# Revit family: Zumtobel LINELIGHT
name_source: partatom
category: Lighting Fixtures
revit_build: Autodesk Revit 2018 (Build: 20170223_1515(x64)
units: mm (PartAtom-declared; Revit-internal decimal feet)

## family parameters
Cut with Voids When Loaded = No
Host = Face
Light Source = Yes
OmniClass Number = 23.80.70.11
OmniClass Title = Luminaries for Internal Lighting
Part Type = Normal
Room Calculation Point = No
Round Connector Dimension = Use Diameter
Shared = No

## types (10) — shared parameters
Assembly Code = D5020210
Body = ZG_Metal_Aluminium
Color Filter = 16777215
Description = LED light line luminaire
Dimming Lamp Color Temperature Shift = <None>
Emit Shape Visible in Rendering = No
Height = 27 mm  [stored 0.0885827 ft]
Lamp = LED
Manufacturer = Zumtobel Lighting
URL = http://www.zumtobel.com
Voltage = 230 V
Width = 60 mm  [stored 0.19685 ft]
zero-valued in all types: Default Elevation

## per-type parameters (varying)
| type | Apparent Load | Emit from Rectangle Length | Emit from Rectangle Width | Length | Model | Photometric Web File | Tilt Angle |
| LINELIGHT L910 | 15 VA | 25 mm  [stored 0.082021 ft] | 900 mm  [stored 2.95276 ft] | 910 mm | 21013707 | 21013707_(STD_LEO).IES | 90.00° |
| AMPHIBIA S 4600 MB | 31 VA | 60 mm  [stored 0.19685 ft] | 1090 mm  [stored 3.57612 ft] | 1100 mm | 42929203 | D39911AA_AMP_S_4600-840_PC_MB.IES | -90.00° |
| AMPHIBIA L 4600 WB | 33 VA | 60 mm  [stored 0.19685 ft] | 1590 mm | 1600 mm  [stored 5.24934 ft] | 42929225 | D39805AA_AMP_L_4600-840_PC_WB.IES | -90.00° |
| AMPHIBIA L 6400 MB | 44 VA | 60 mm  [stored 0.19685 ft] | 1590 mm | 1600 mm  [stored 5.24934 ft] | 42929253 | D39911AA_AMP_L_6400-840_PC_MB.IES | -90.00° |
| AMPHIBIA L 6400 NB | 41 VA | 60 mm  [stored 0.19685 ft] | 1590 mm | 1600 mm  [stored 5.24934 ft] | 42929257 | D39907AA_AMP_L_6400-840_PC_NB.IES | -90.00° |
| AMPHIBIA L 6400 WB | 46 VA | 60 mm  [stored 0.19685 ft] | 1590 mm | 1600 mm  [stored 5.24934 ft] | 42929249 | D39805AA_AMP_L_6400-840_PC_WB.IES | -90.00° |
| AMPHIBIA L 8000 MB | 58 VA | 60 mm  [stored 0.19685 ft] | 1590 mm | 1600 mm  [stored 5.24934 ft] | 42929288 | D39911AA_AMP_L_8000-840_PC_MB.IES | -90.00° |
| AMPHIBIA L 8000 NB | 53 VA | 60 mm  [stored 0.19685 ft] | 1590 mm | 1600 mm  [stored 5.24934 ft] | 42929292 | D39907AA_AMP_L_8000-840_PC_NB.IES | -90.00° |
| AMPHIBIA L 8000 WB | 59 VA | 60 mm  [stored 0.19685 ft] | 1590 mm | 1600 mm  [stored 5.24934 ft] | 42929284 | D39805AA_AMP_L_8000-840_PC_WB.IES | -90.00° |
| AMPHIBIA S 4600 WB | 32 VA | 60 mm  [stored 0.19685 ft] | 1090 mm  [stored 3.57612 ft] | 1100 mm | 42929199 | D39805AA_AMP_S_4600-840_PC_WB.IES | -90.00° |

note: [stored X ft] marks values corroborated as IEEE doubles in the binary element streams (Revit-internal decimal feet)

## geometry (parser evidence)
native form markers: Sweep x2
no freeform markers — native parametric forms only
